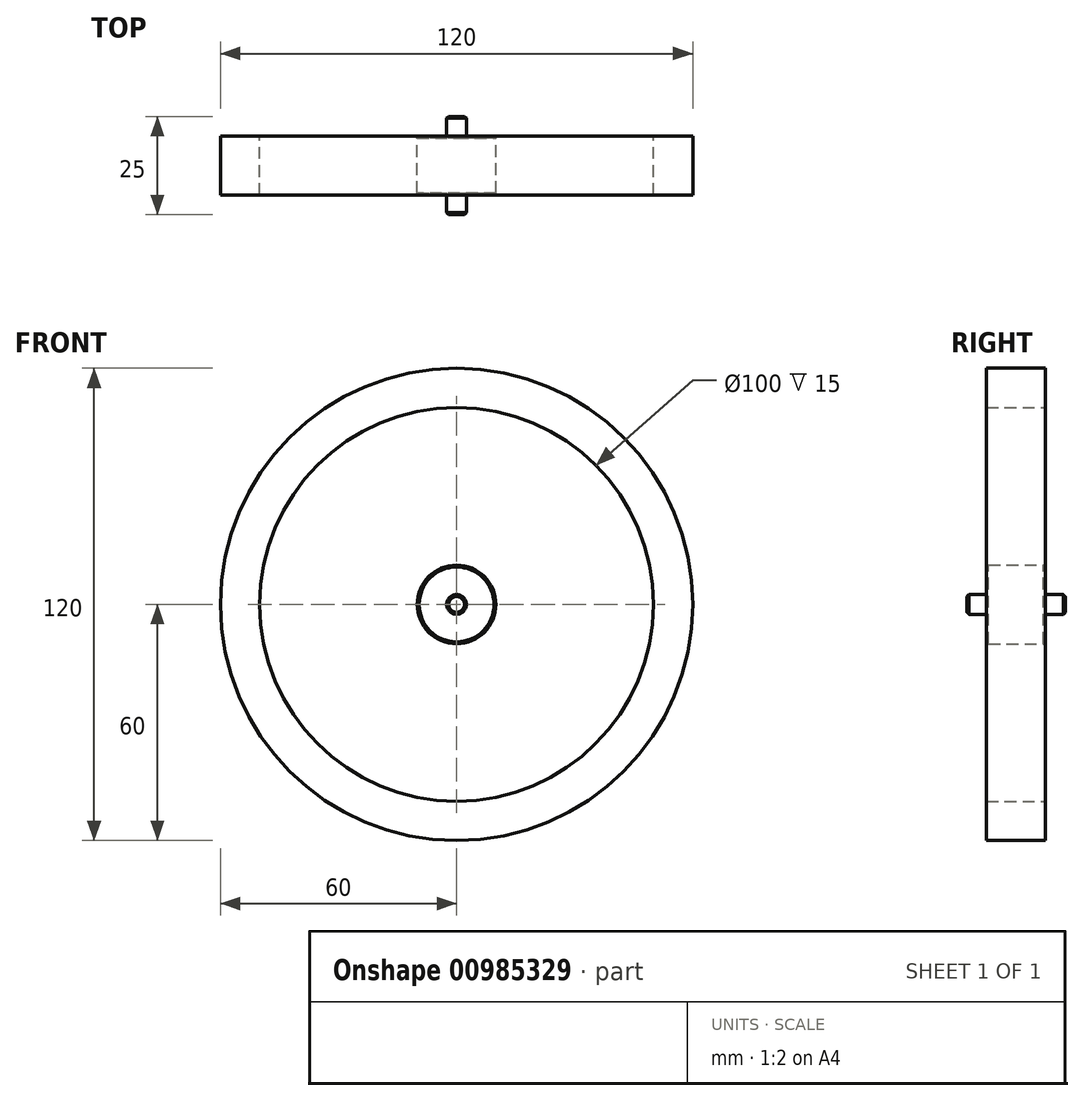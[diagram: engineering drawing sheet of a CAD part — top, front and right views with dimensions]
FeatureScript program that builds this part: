
annotation { "Feature Type Name" : "Feature", "Feature Type Description" : "" }
export const myFeature = defineFeature(function(context is Context, id is Id, definition is map)
    precondition{}
    {
        {
            var Q0;
            Q0=qCreatedBy(makeId("Front.planeOp"),FACE);
            var sketch = newSketch(context, id + "F0", { "sketchPlane" : qUnion([Q0])});
            skCircle(sketch, "E0", {"center": v(0, 0) * mm, "radius": 50 * mm});
            skCircle(sketch, "E1", {"center": v(0, 0) * mm, "radius": 60 * mm});
            skCircle(sketch, "E2", {"center": v(0, 0) * mm, "radius": 10 * mm});
            skSolve(sketch);
        }
        {
            var Q0;
            Q0=makeQuery(id+"F0.imprint","IMPRINT",FACE,{"disambiguationData":[TD([[makeQuery(id+"F0.imprint","IMPRINT",EDGE,{"derivedFrom":sQuery(id+"F0.wireOp",EDGE,"E0")}),-1.0]])]});
            var Q1;
            Q1=makeQuery(id+"F0.imprint","IMPRINT",FACE,{"disambiguationData":[TD([[makeQuery(id+"F0.imprint","IMPRINT",EDGE,{"derivedFrom":sQuery(id+"F0.wireOp",EDGE,"E2")}),1.0]])]});
            var Q2;
            Q2=makeQuery(id+"F0.imprint","IMPRINT",FACE,{"disambiguationData":[TD([[makeQuery(id+"F0.imprint","IMPRINT",EDGE,{"derivedFrom":sQuery(id+"F0.wireOp",EDGE,"J92ynaHh-N60y-aWHb-ryBn-4pcqnySto3lE")}),1.0]])]});
            extrude(context, id + "F1", {"entities" : qUnion([Q0, Q1, Q2]), "depth" : 15 * mm, "offsetDistance" : 25 * mm});
        }
        {
            var Q0;
            Q0=makeQuery(id+"F1.opExtrude","CAP_FACE",FACE,{"disambiguationData":[OSD([sQuery(id+"F0.wireOp",EDGE,"E2")])],"isStart":false});
            var sketch = newSketch(context, id + "F2", { "sketchPlane" : qUnion([Q0])});
            skCircle(sketch, "E3", {"center": v(0, 0) * mm, "radius": 2.5 * mm});
            skSolve(sketch);
        }
        {
            var Q0;
            Q0=makeQuery(id+"F2.imprint","IMPRINT",FACE,{"disambiguationData":[TD([[makeQuery(id+"F2.imprint","IMPRINT",EDGE,{"derivedFrom":sQuery(id+"F2.wireOp",EDGE,"E3")}),1.0]])]});
            extrude(context, id + "F3", {"entities" : qUnion([Q0]), "operationType" : NewBodyOperationType.ADD, "depth" : 5 * mm, "offsetDistance" : 25 * mm});
        }
        {
            var Q0;
            Q0=makeQuery(id+"F1.opExtrude","CAP_FACE",FACE,{"disambiguationData":[OSD([sQuery(id+"F0.wireOp",EDGE,"E2")])],"isStart":true});
            var sketch = newSketch(context, id + "F4", { "sketchPlane" : qUnion([Q0])});
            skCircle(sketch, "E4", {"center": v(0, 0) * mm, "radius": 2.5 * mm});
            skSolve(sketch);
        }
        {
            var Q0;
            Q0=makeQuery(id+"F4.imprint","IMPRINT",FACE,{"disambiguationData":[TD([[makeQuery(id+"F4.imprint","IMPRINT",EDGE,{"derivedFrom":sQuery(id+"F4.wireOp",EDGE,"E4")}),1.0]])]});
            extrude(context, id + "F5", {"entities" : qUnion([Q0]), "operationType" : NewBodyOperationType.ADD, "depth" : 5 * mm, "offsetDistance" : 25 * mm});
        }
        {
            var Q0;
            Q0=makeQuery(id+"F3.opExtrude","CAP_EDGE",EDGE,{"disambiguationData":[OSD([sQuery(id+"F2.wireOp",EDGE,"E3")])],"isStart":false});
            chamfer(context, id + "F6", {"entities" : qUnion([Q0]), "width" : 0.5 * mm, "tangentPropagation" : true});
        }
        {
            var Q0;
            Q0=makeQuery(id+"F1.opExtrude","SWEPT_FACE",FACE,{"disambiguationData":[OSD([sQuery(id+"F0.wireOp",EDGE,"E2")])]});
            var Q1;
            Q1=makeQuery(id+"F1.opExtrude","CAP_EDGE",EDGE,{"disambiguationData":[OSD([sQuery(id+"F0.wireOp",EDGE,"E2")])],"isStart":false});
            chamfer(context, id + "F7", {"entities" : qUnion([Q0, Q1]), "width" : 0.5 * mm, "tangentPropagation" : true});
        }
        {
            var Q0;
            Q0=makeQuery(id+"F5.opExtrude","CAP_EDGE",EDGE,{"disambiguationData":[OSD([sQuery(id+"F4.wireOp",EDGE,"E4")])],"isStart":false});
            chamfer(context, id + "F8", {"entities" : qUnion([Q0]), "width" : 0.5 * mm, "tangentPropagation" : true});
        }
    });
